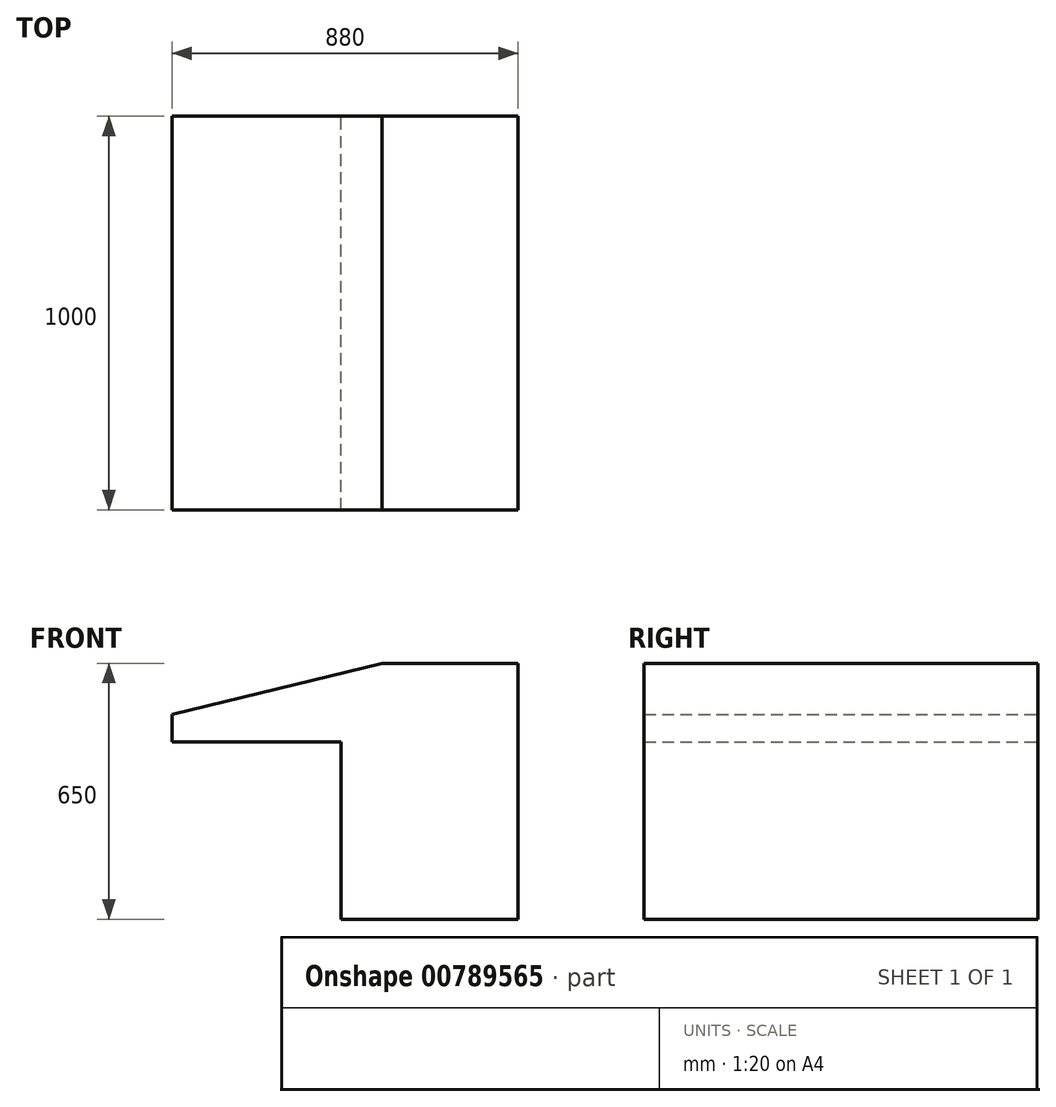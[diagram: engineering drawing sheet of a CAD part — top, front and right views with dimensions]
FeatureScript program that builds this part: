
annotation { "Feature Type Name" : "Feature", "Feature Type Description" : "" }
export const myFeature = defineFeature(function(context is Context, id is Id, definition is map)
    precondition{}
    {
        {
            var Q0;
            Q0=qCreatedBy(makeId("Front.planeOp"),FACE);
            var sketch = newSketch(context, id + "F0", { "sketchPlane" : qUnion([Q0])});
            skLineSegment(sketch, "E0", {"start": v(-20.51, -43.42) * mm, "end": v(429.49, -43.42) * mm});
            skLineSegment(sketch, "E1", {"start": v(-20.51, -43.42) * mm, "end": v(-20.51, -93.42) * mm});
            skLineSegment(sketch, "E2", {"start": v(-20.51, -93.42) * mm, "end": v(429.49, -93.42) * mm});
            skLineSegment(sketch, "E3", {"start": v(429.49, -93.42) * mm, "end": v(429.49, -43.42) * mm});
            skLineSegment(sketch, "E4", {"start": v(429.49, -43.42) * mm, "end": v(429.49, 556.58) * mm});
            skLineSegment(sketch, "E5", {"start": v(-20.51, -43.42) * mm, "end": v(-20.51, 356.58) * mm});
            skLineSegment(sketch, "E6", {"start": v(-20.51, 356.58) * mm, "end": v(-450.51, 356.58) * mm});
            skLineSegment(sketch, "E7", {"start": v(-450.51, 356.58) * mm, "end": v(-450.51, 426.58) * mm});
            skLineSegment(sketch, "E8", {"start": v(-450.51, 426.58) * mm, "end": v(83.9, 556.58) * mm});
            skLineSegment(sketch, "E9", {"start": v(83.9, 556.58) * mm, "end": v(429.49, 556.58) * mm});
            skSolve(sketch);
        }
        {
            var Q0;
            Q0 = qSketchRegion(id + "F0", true);
            extrude(context, id + "F1", {"entities" : qUnion([Q0]), "depth" : 500 * mm, "offsetDistance" : 25 * mm, "hasSecondDirection" : true, "secondDirectionOppositeDirection" : true, "secondDirectionDepth" : 500 * mm});
        }
    });
